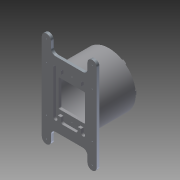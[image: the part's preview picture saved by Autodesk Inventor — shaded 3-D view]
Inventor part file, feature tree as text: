
AUTODESK INVENTOR PART (.ipt)
format: ipt  version: 2015 (Build 190159000, 159)  size: 447,488 bytes
history: native  units: in
note: dims shown in document units (in); Inventor stores cm internally (conversion verified against a paired STEP export)
features: direct_edit x5, move_body x5, other x4, extrude x3, sketch x3, imported_body x2, boolean_combine x1, reference x1
ambient origin geometry x8: Origin, YZ Plane, XZ Plane, XY Plane, X Axis, Y Axis, Z Axis, Center Point
bodies: Solid2 (feature_tree)
feature tree (24):
  other  "BetaSkeletonV011"
  direct_edit  "Direct Edit1"
  direct_edit  "Direct Edit2"
  extrude  "Extrusion1"  Depth=0.0394in
  direct_edit  "Direct Edit4"
  direct_edit  "Direct Edit5"
  direct_edit  "Direct Edit6"
  imported_body  "Base2"
  boolean_combine  "Combine1"
  extrude  "Extrusion2"  Depth=0.0059in TaperAngle=0.0deg
  extrude  "Extrusion3"  Depth=0.1969in
  imported_body  "Base1"
  sketch  "Sketch1"  dims[d0=0.0394in d1=0.0394in]
  sketch  "Sketch2"  dims[d2=0.0in d3=0.0in d4=-0.1378in d8=0.0in d9=0.0in d10=0.0059in]
  reference  "Reference1"
  sketch  "Sketch3"  dims[d11=0.0in d12=0.0in d13=0.0059in d14=2.2835in d15=1.3976in d16=0.0in d17=0.0in d18=0.0in d19=-0.125in d20=0.0in d21=0.0in d22=-0.125in d23=0.1969in d24=0.1969in d25=2.3622in d26=0.0in d27=1.1811in d28=1.1811in d29=2.3622in d30=0.0in]
  other  "Size1"
  other  "Size2"
  move_body  "Move1"
  move_body  "Move3"
  move_body  "Move4"
  other  "Size3"
  move_body  "Move5"
  move_body  "Move6"
